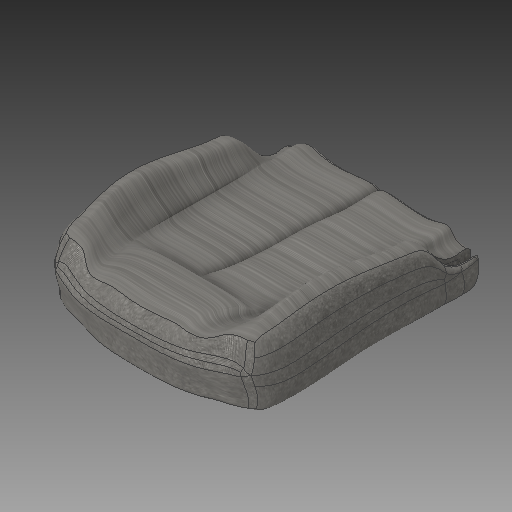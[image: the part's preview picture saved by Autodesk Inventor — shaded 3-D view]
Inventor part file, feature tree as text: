
AUTODESK INVENTOR PART (.ipt)
format: ipt  version: 2019 (Build 230136000, 136)  size: 2,389,504 bytes
history: native  units: in
note: dims shown in document units (in); Inventor stores cm internally (conversion verified against a paired STEP export)
features: sketch x13, other x10, extrude x10, fillet x6, plane x5, projected_geometry x3, mirror x2
ambient origin geometry x8: Origin, YZ Plane, XZ Plane, XY Plane, X Axis, Y Axis, Z Axis, Center Point
bodies: Solid1 (feature_tree)
feature tree (49):
  other  "Blocks"
  plane  "Work Plane1"
  plane  "Work Plane2"
  plane  "Work Plane3"
  plane  "Work Plane4"
  other  "Form1"
  sketch  "Sketch1"  dims[d0=7.874in d3=3.248in]
  sketch  "Sketch3"  dims[d4=9.8425in d5=-0.1772in]
  sketch  "Sketch4"  dims[d11=13.3858in d12=0.0in d13=0.7874in]
  sketch  "Sketch5"  dims[d14=23.622in d15=1.9685in]
  sketch  "Sketch8"  dims[d16=0.0in d17=0.0in d18=0.3937in]
  extrude  "Extrusion3"  Depth=3.248in
  extrude  "Extrusion4"  [1 undecoded]
  extrude  "Extrusion5"  Depth=0.7874in
  extrude  "Extrusion7"  Depth=1.9685in
  mirror  "Mirror1"
  extrude  "Extrusion8"  Depth=0.3937in
  extrude  "Extrusion9"  TaperAngle=0.0deg  [1 undecoded]
  mirror  "Mirror2"
  extrude  "Extrusion10"  Depth=6.6929in
  fillet  "Fillet1"  Radius=2.3622in
  fillet  "Fillet2"  Radius=3.937in
  fillet  "Fillet3"  Radius=0.5906in
  fillet  "Fillet4"  Radius=0.0394in
  fillet  "Fillet5"  Radius=1.1811in
  extrude  "Extrusion11"  Depth=0.7874in
  extrude  "Extrusion12"  Depth=0.1969in
  fillet  "Fillet6"  Radius=0.1969in
  plane  "Work Plane5"
  extrude  "Extrusion13"  Depth=0.3937in TaperAngle=0.0deg
  other  "Block1"
  other  "Block2"
  other  "Block3"
  other  "Block4"
  other  "Block5"
  sketch  "Sketch9"  dims[d20=1.1811in d21=0.0in d24=0.0in d25=0.0in]
  sketch  "Sketch10"  dims[d26=0.7874in d27=6.6929in d28=2.3622in d29=0.0in d30=3.937in d31=0.5906in d32=0.0394in d33=1.1811in d34=0.0in]
  other  "Block6"
  projected_geometry  "Projected Loop1"
  sketch  "Sketch12"  dims[d35=1.1811in d36=0.0in d37=0.7874in]
  sketch  "Sketch13"  dims[d38=0.7874in d39=0.1969in d40=0.1969in]
  sketch  "Sketch14"  dims[d41=0.1969in d42=0.3937in d43=0.0in]
  projected_geometry  "Projected Loop3"
  sketch  "Sketch15"  dims[d44=0.5906in d45=0.1969in d46=0.0in d47=0.0in]
  sketch  "Sketch16"  dims[d48=0.0787in]
  projected_geometry  "Projected Loop4"
  sketch  "Sketch17"  dims[d49=-9.8425in d50=2.1654in d51=0.0in d52=1.1024in d53=1.1024in]
  other  "Block2:1"
  other  "Block3:1"
note: 2 required parameter values undecoded (feature->parameter linkage not recoverable at this tier; creation-order binding heuristic only, values carry confidence <= 0.55)
